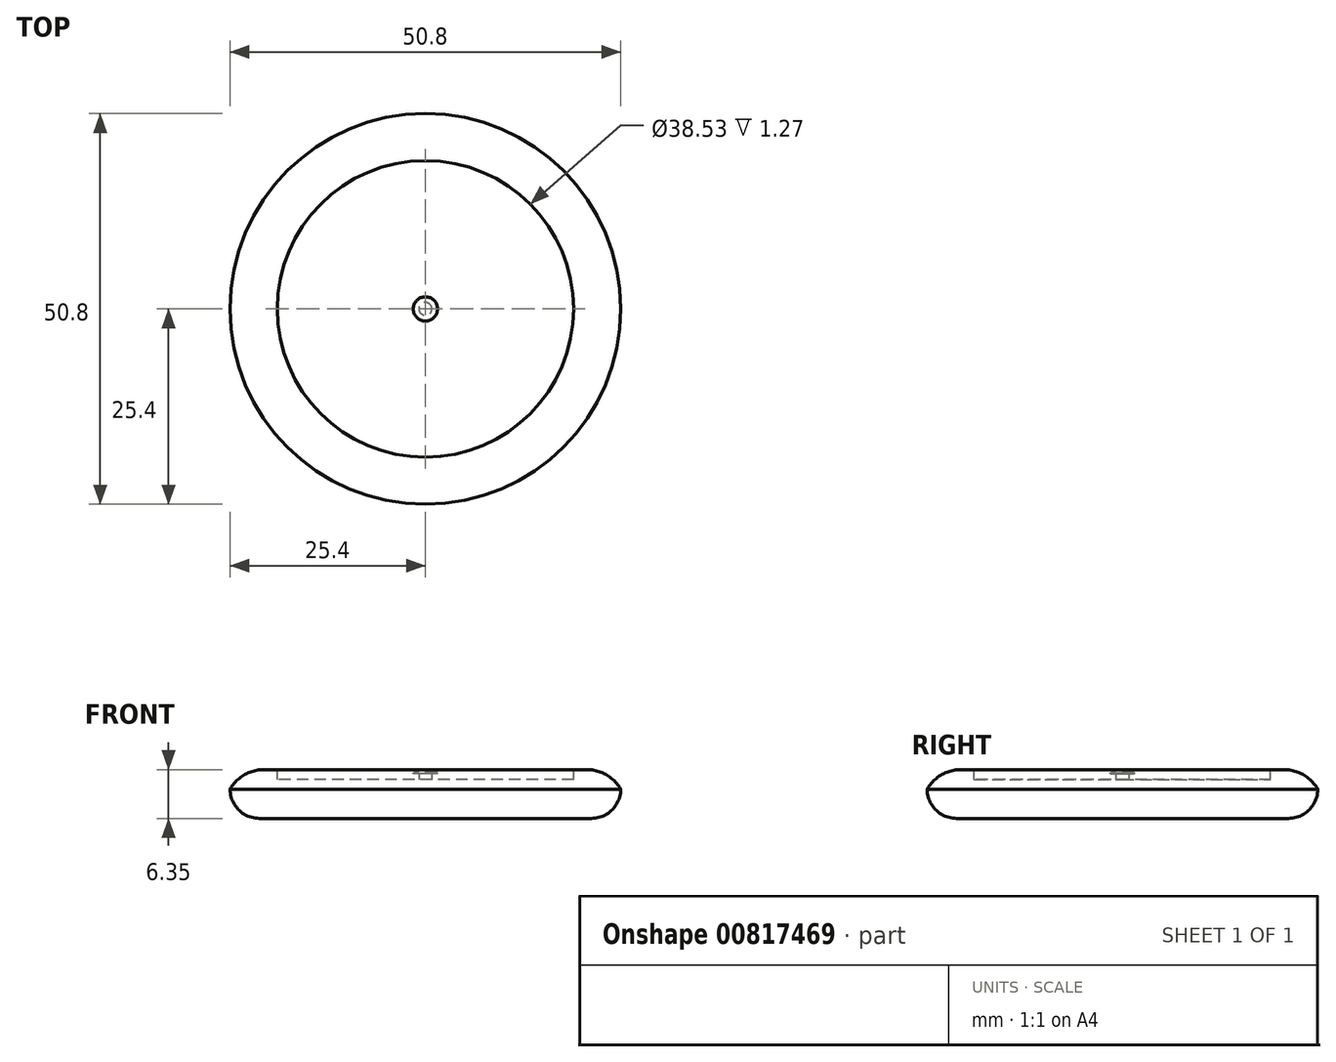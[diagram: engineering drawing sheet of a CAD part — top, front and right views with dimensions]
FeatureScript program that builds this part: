
annotation { "Feature Type Name" : "Feature", "Feature Type Description" : "" }
export const myFeature = defineFeature(function(context is Context, id is Id, definition is map)
    precondition{}
    {
        {
            var Q0;
            Q0=qCreatedBy(makeId("Top.planeOp"),FACE);
            var sketch = newSketch(context, id + "F0", { "sketchPlane" : qUnion([Q0])});
            skCircle(sketch, "E0", {"center": v(0, 0) * mm, "radius": 25.4 * mm});
            skSolve(sketch);
        }
        {
            var Q0;
            Q0=makeQuery(id+"F0.imprint","IMPRINT",FACE,{"disambiguationData":[TD([[makeQuery(id+"F0.imprint","IMPRINT",EDGE,{"derivedFrom":sQuery(id+"F0.wireOp",EDGE,"E0")}),1.0]])]});
            extrude(context, id + "F1", {"entities" : qUnion([Q0]), "depth" : 6.35 * mm, "offsetDistance" : 25.4 * mm});
        }
        {
            var Q0;
            Q0=makeQuery(id+"F1.opExtrude","CAP_EDGE",EDGE,{"disambiguationData":[OSD([sQuery(id+"F0.wireOp",EDGE,"E0")])],"isStart":true});
            fillet(context, id + "F2", {"entities" : qUnion([Q0]), "radius" : 3.8 * mm, "tangentPropagation" : true, "allowEdgeOverflow" : false});
        }
        {
            var Q0;
            Q0=makeQuery(id+"F1.opExtrude","CAP_EDGE",EDGE,{"disambiguationData":[OSD([sQuery(id+"F0.wireOp",EDGE,"E0")])],"isStart":false});
            fillet(context, id + "F3", {"entities" : qUnion([Q0]), "radius" : 5.08 * mm, "tangentPropagation" : true, "allowEdgeOverflow" : false});
        }
        {
            var Q0;
            Q0=makeQuery(id+"F1.opExtrude","CAP_FACE",FACE,{"disambiguationData":[OSD([sQuery(id+"F0.wireOp",EDGE,"E0")])],"isStart":false});
            var sketch = newSketch(context, id + "F4", { "sketchPlane" : qUnion([Q0])});
            skCircle(sketch, "E1", {"center": v(0, 0) * mm, "radius": 19.27 * mm});
            skSolve(sketch);
        }
        {
            var Q0;
            Q0 = qSketchRegion(id + "F4", true);
            extrude(context, id + "F5", {"entities" : qUnion([Q0]), "operationType" : NewBodyOperationType.REMOVE, "oppositeDirection" : true, "depth" : 1.27 * mm, "offsetDistance" : 25.4 * mm});
        }
        {
            var Q0;
            Q0=makeQuery(id+"F5.boolean.opBoolean","COPY",FACE,{"derivedFrom":makeQuery(id+"F5.opExtrude","CAP_FACE",FACE,{"disambiguationData":[OSD([sQuery(id+"F4.wireOp",EDGE,"E1")])],"isStart":false})});
            var sketch = newSketch(context, id + "F6", { "sketchPlane" : qUnion([Q0])});
            skCircle(sketch, "E2", {"center": v(0, 0) * mm, "radius": 0.84 * mm});
            skSolve(sketch);
        }
        {
            var Q0;
            Q0=makeQuery(id+"F6.imprint","IMPRINT",FACE,{"disambiguationData":[TD([[makeQuery(id+"F6.imprint","IMPRINT",EDGE,{"derivedFrom":sQuery(id+"F6.wireOp",EDGE,"E2")}),1.0]])]});
            extrude(context, id + "F7", {"entities" : qUnion([Q0]), "operationType" : NewBodyOperationType.ADD, "depth" : 0.76 * mm, "offsetDistance" : 25.4 * mm});
        }
        {
            var Q0;
            Q0=makeQuery(id+"F7.opExtrude","CAP_FACE",FACE,{"disambiguationData":[OSD([sQuery(id+"F6.wireOp",EDGE,"E2")])],"isStart":false});
            var sketch = newSketch(context, id + "F8", { "sketchPlane" : qUnion([Q0])});
            skCircle(sketch, "E3", {"center": v(0, 0) * mm, "radius": 1.57 * mm});
            skSolve(sketch);
        }
        {
            var Q0;
            Q0=makeQuery(id+"F8.imprint","IMPRINT",FACE,{"disambiguationData":[TD([[makeQuery(id+"F8.imprint","IMPRINT",EDGE,{"derivedFrom":sQuery(id+"F8.wireOp",EDGE,"E3")}),1.0]])]});
            var Q1;
            Q1=makeQuery(id+"F8.imprint","IMPRINT",FACE,{"disambiguationData":[TD([[makeQuery(id+"F8.imprint","IMPRINT",EDGE,{"derivedFrom":makeQuery(id+"F7.opExtrude","CAP_EDGE",EDGE,{"disambiguationData":[OSD([sQuery(id+"F6.wireOp",EDGE,"E2")])],"isStart":false})}),1.0]])]});
            extrude(context, id + "F9", {"entities" : qUnion([Q0, Q1]), "operationType" : NewBodyOperationType.ADD, "depth" : 0.13 * mm, "offsetDistance" : 25.4 * mm});
        }
        {
            var Q0;
            Q0=makeQuery(id+"F9.opExtrude","CAP_EDGE",EDGE,{"disambiguationData":[OSD([sQuery(id+"F8.wireOp",EDGE,"E3")])],"isStart":false});
            fillet(context, id + "F10", {"entities" : qUnion([Q0]), "radius" : 0.13 * mm, "tangentPropagation" : true, "allowEdgeOverflow" : false});
        }
    });
